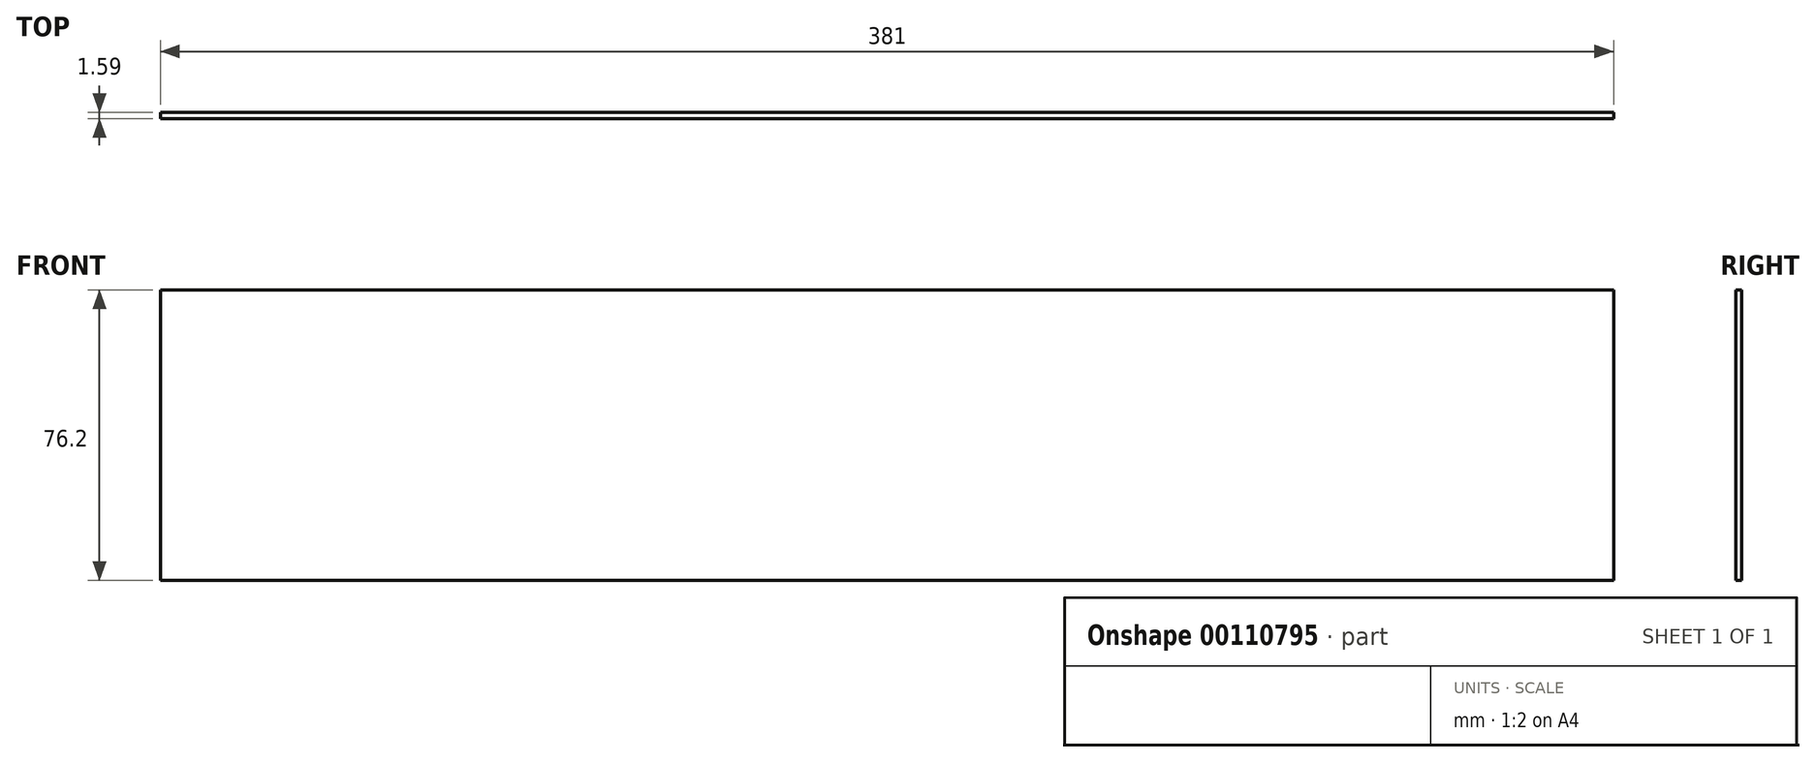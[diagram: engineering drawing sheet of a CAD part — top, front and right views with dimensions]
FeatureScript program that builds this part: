
annotation { "Feature Type Name" : "Feature", "Feature Type Description" : "" }
export const myFeature = defineFeature(function(context is Context, id is Id, definition is map)
    precondition{}
    {
        {
            var Q0;
            Q0=qCreatedBy(makeId("Front.planeOp"),FACE);
            var sketch = newSketch(context, id + "F0", { "sketchPlane" : qUnion([Q0])});
            skLineSegment(sketch, "E0.bottom", {"start": v(-161.04, 36.88) * mm, "end": v(219.96, 36.88) * mm});
            skLineSegment(sketch, "E0.top", {"start": v(-161.04, -39.32) * mm, "end": v(219.96, -39.32) * mm});
            skLineSegment(sketch, "E0.left", {"start": v(-161.04, 36.88) * mm, "end": v(-161.04, -39.32) * mm});
            skLineSegment(sketch, "E0.right", {"start": v(219.96, 36.88) * mm, "end": v(219.96, -39.32) * mm});
            skSolve(sketch);
        }
        {
            var Q0;
            Q0=makeQuery(id+"F0.imprint","IMPRINT",FACE,{"disambiguationData":[TD([[makeQuery(id+"F0.imprint","IMPRINT",EDGE,{"derivedFrom":sQuery(id+"F0.wireOp",EDGE,"E0.bottom")}),-1.0]])]});
            extrude(context, id + "F1", {"entities" : qUnion([Q0]), "depth" : 1.59 * mm});
        }
    });
